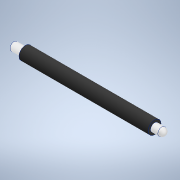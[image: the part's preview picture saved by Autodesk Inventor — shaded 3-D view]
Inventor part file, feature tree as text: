
AUTODESK INVENTOR PART (.ipt)
format: ipt  version: 2022 (Build 260153000, 153)  size: 115,712 bytes
history: native  units: in
note: dims shown in document units (in); Inventor stores cm internally (conversion verified against a paired STEP export)
features: extrude x3, sketch x3, fillet x1
ambient origin geometry x8: Origin, YZ Plane, XZ Plane, XY Plane, X Axis, Y Axis, Z Axis, Center Point
bodies: Solid1 (feature_tree)
feature tree (7):
  extrude  "Extrusion1"  Depth=1.0in TaperAngle=0.0deg
  extrude  "Extrusion2"  Depth=0.0875in TaperAngle=0.0deg
  extrude  "Extrusion3"  Depth=0.0875in TaperAngle=0.0deg
  fillet  "Fillet1"  Radius=0.0312in
  sketch  "Sketch1"  dims[d0=0.1in d1=1.0in d2=0.0in]
  sketch  "Sketch2"  dims[d3=0.0625in d4=0.0875in d5=0.0in]
  sketch  "Sketch3"  dims[d6=0.0625in d7=0.0875in d8=0.0in d9=0.0312in]
